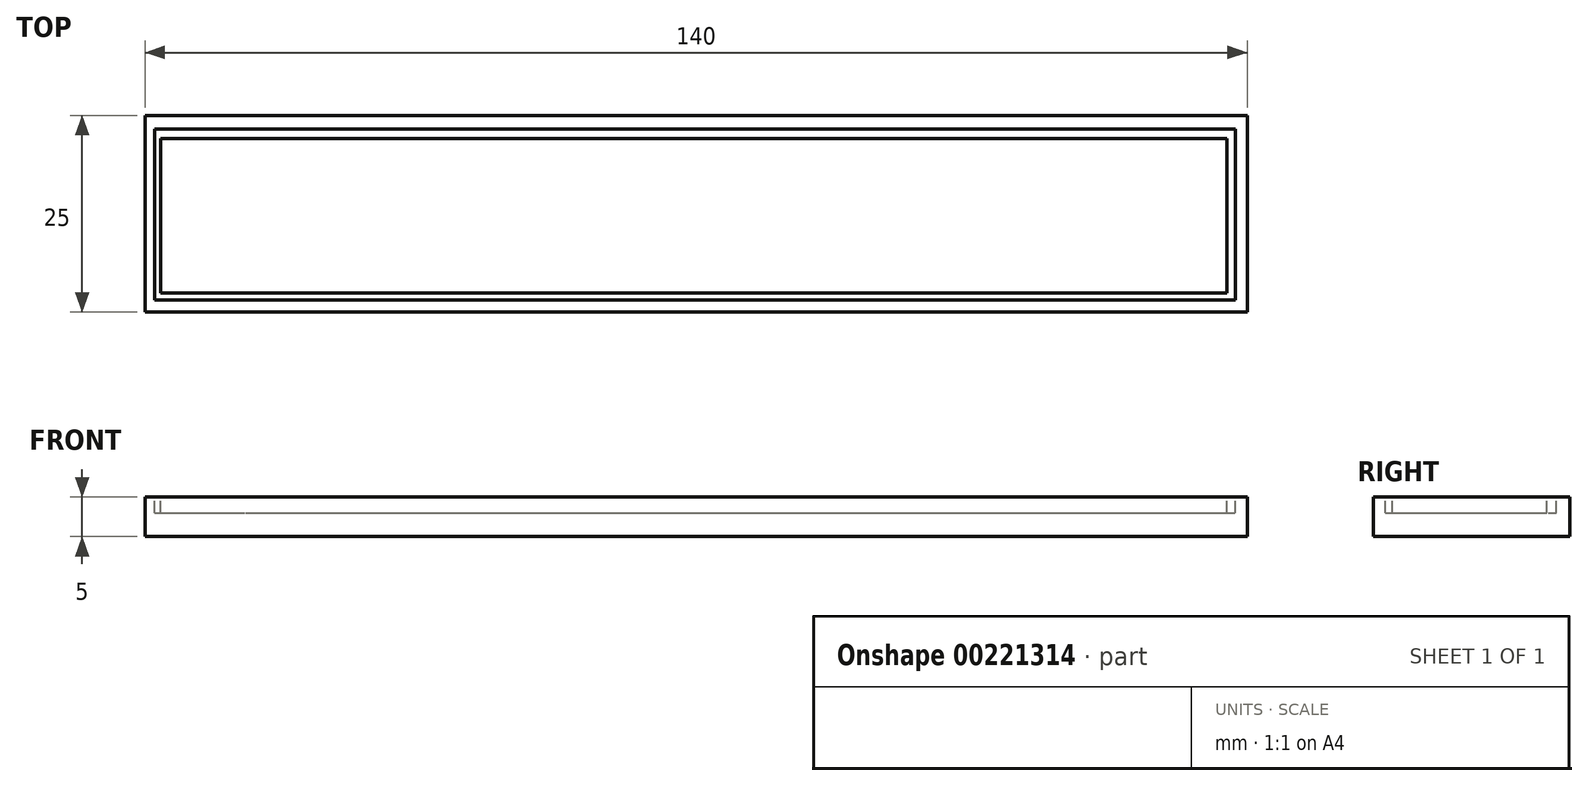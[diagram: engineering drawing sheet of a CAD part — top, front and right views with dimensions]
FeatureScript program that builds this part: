
annotation { "Feature Type Name" : "Feature", "Feature Type Description" : "" }
export const myFeature = defineFeature(function(context is Context, id is Id, definition is map)
    precondition{}
    {
        {
            var Q0;
            Q0=qCreatedBy(makeId("Top.planeOp"),FACE);
            var sketch = newSketch(context, id + "F0", { "sketchPlane" : qUnion([Q0])});
            skLineSegment(sketch, "E0.bottom", {"start": v(-44.1, -35.9) * mm, "end": v(95.9, -35.9) * mm});
            skLineSegment(sketch, "E0.top", {"start": v(-44.1, -10.9) * mm, "end": v(95.9, -10.9) * mm});
            skLineSegment(sketch, "E0.left", {"start": v(-44.1, -35.9) * mm, "end": v(-44.1, -10.9) * mm});
            skLineSegment(sketch, "E0.right", {"start": v(95.9, -35.9) * mm, "end": v(95.9, -10.9) * mm});
            skSolve(sketch);
        }
        {
            var Q0;
            Q0=makeQuery(id+"F0.imprint","IMPRINT",FACE,{"disambiguationData":[TD([[makeQuery(id+"F0.imprint","IMPRINT",EDGE,{"derivedFrom":sQuery(id+"F0.wireOp",EDGE,"E0.bottom")}),1.0]])]});
            extrude(context, id + "F1", {"entities" : qUnion([Q0]), "depth" : 5 * mm});
        }
        {
            var Q0;
            Q0=makeQuery(id+"F1.opExtrude","CAP_FACE",FACE,{"disambiguationData":[OSD([sQuery(id+"F0.wireOp",EDGE,"E0.bottom"),sQuery(id+"F0.wireOp",EDGE,"E0.top"),sQuery(id+"F0.wireOp",EDGE,"E0.left"),sQuery(id+"F0.wireOp",EDGE,"E0.right")])],"isStart":false});
            var sketch = newSketch(context, id + "F2", { "sketchPlane" : qUnion([Q0])});
            skLineSegment(sketch, "E1.bottom", {"start": v(-42.87, -34.36) * mm, "end": v(94.4, -34.36) * mm});
            skLineSegment(sketch, "E1.top", {"start": v(-42.87, -12.64) * mm, "end": v(94.4, -12.64) * mm});
            skLineSegment(sketch, "E1.left", {"start": v(-42.87, -34.36) * mm, "end": v(-42.87, -12.64) * mm});
            skLineSegment(sketch, "E1.right", {"start": v(94.4, -34.36) * mm, "end": v(94.4, -12.64) * mm});
            skSolve(sketch);
        }
        {
            var Q0;
            Q0=makeQuery(id+"F2.imprint","IMPRINT",FACE,{"disambiguationData":[TD([[makeQuery(id+"F2.imprint","IMPRINT",EDGE,{"derivedFrom":sQuery(id+"F2.wireOp",EDGE,"E1.bottom")}),1.0]])]});
            var sketch = newSketch(context, id + "F3", { "sketchPlane" : qUnion([Q0])});
            skLineSegment(sketch, "E2.bottom", {"start": v(-42.13, -33.48) * mm, "end": v(93.3, -33.48) * mm});
            skLineSegment(sketch, "E2.top", {"start": v(-42.13, -13.85) * mm, "end": v(93.3, -13.85) * mm});
            skLineSegment(sketch, "E2.left", {"start": v(-42.13, -33.48) * mm, "end": v(-42.13, -13.85) * mm});
            skLineSegment(sketch, "E2.right", {"start": v(93.3, -33.48) * mm, "end": v(93.3, -13.85) * mm});
            skSolve(sketch);
        }
        {
            var Q0;
            Q0=makeQuery(id+"F2.imprint","IMPRINT",FACE,{"disambiguationData":[TD([[makeQuery(id+"F2.imprint","IMPRINT",EDGE,{"derivedFrom":sQuery(id+"F2.wireOp",EDGE,"E1.bottom")}),1.0]])]});
            extrude(context, id + "F4", {"entities" : qUnion([Q0]), "operationType" : NewBodyOperationType.REMOVE, "depth" : 2 * mm});
        }
        {
            var Q0;
            Q0=makeQuery(id+"F3.imprint","IMPRINT",FACE,{"disambiguationData":[TD([[makeQuery(id+"F3.imprint","IMPRINT",EDGE,{"derivedFrom":sQuery(id+"F3.wireOp",EDGE,"E2.bottom")}),-1.0]])]});
            extrude(context, id + "F5", {"entities" : qUnion([Q0]), "operationType" : NewBodyOperationType.REMOVE, "oppositeDirection" : true, "depth" : 2 * mm});
        }
    });
